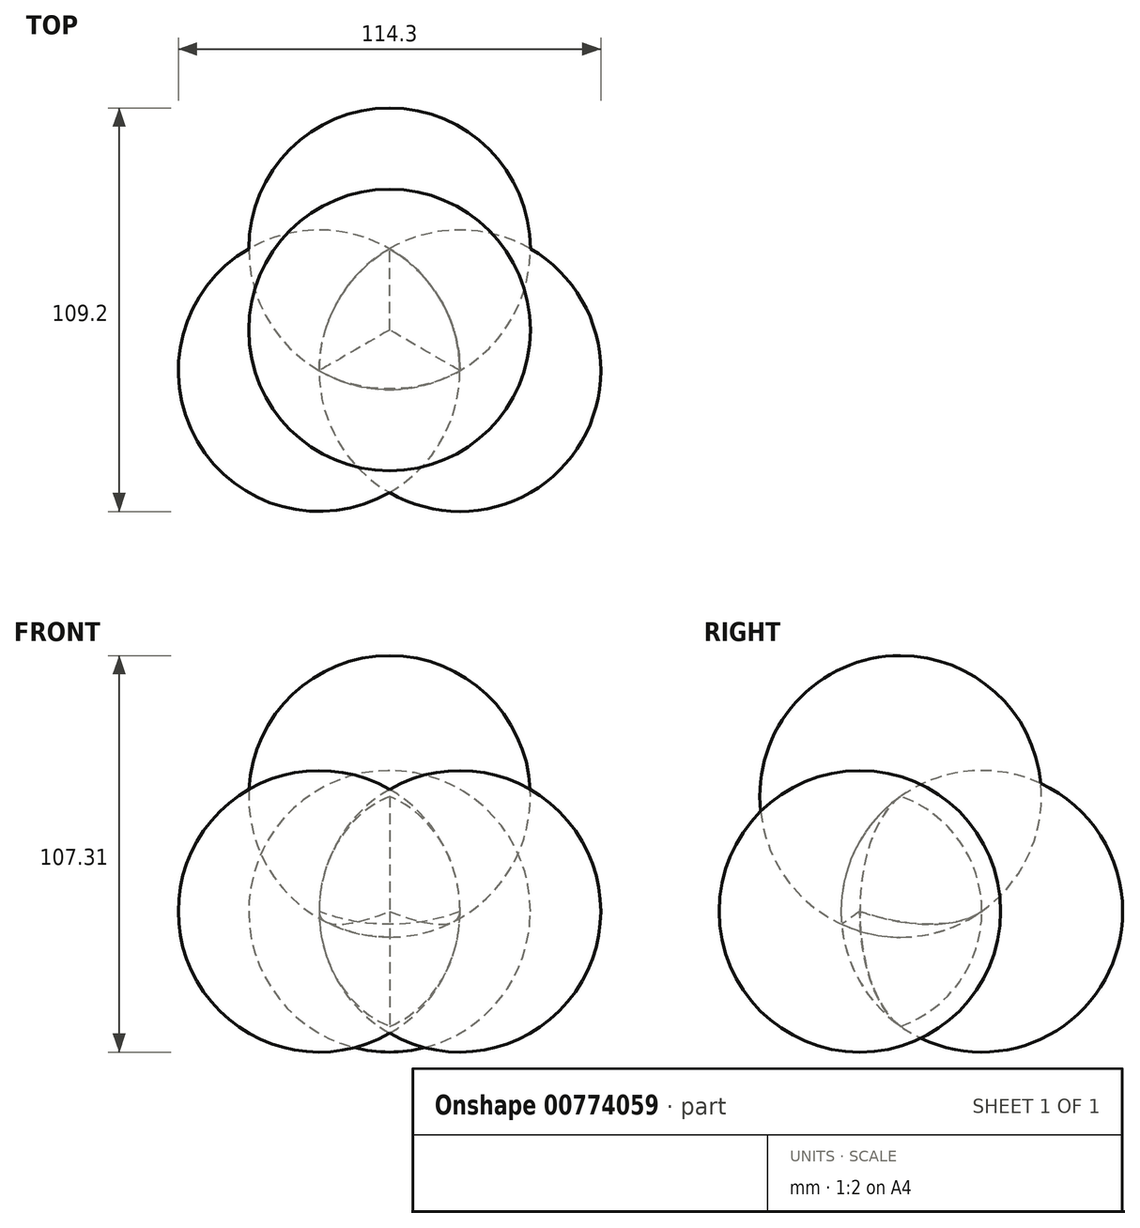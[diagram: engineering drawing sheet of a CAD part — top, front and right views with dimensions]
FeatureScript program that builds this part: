
annotation { "Feature Type Name" : "Feature", "Feature Type Description" : "" }
export const myFeature = defineFeature(function(context is Context, id is Id, definition is map)
    precondition{}
    {
        {
            var Q0;
            Q0=qCreatedBy(makeId("Top.planeOp"),FACE);
            var sketch = newSketch(context, id + "F0", { "sketchPlane" : qUnion([Q0])});
            skLineSegment(sketch, "E0", {"start": v(-19.05, -11) * mm, "end": v(0, 22) * mm, "construction": true});
            skLineSegment(sketch, "E1", {"start": v(0, 22) * mm, "end": v(19.05, -11) * mm, "construction": true});
            skLineSegment(sketch, "E2", {"start": v(19.05, -11) * mm, "end": v(-19.05, -11) * mm, "construction": true});
            skLineSegment(sketch, "E3", {"start": v(0, 0) * mm, "end": v(-19.05, -11) * mm, "construction": true});
            skLineSegment(sketch, "E4", {"start": v(0, 0) * mm, "end": v(0, 22) * mm, "construction": true});
            skLineSegment(sketch, "E5", {"start": v(0, 0) * mm, "end": v(19.05, -11) * mm, "construction": true});
            skSolve(sketch);
        }
        {
            var Q0;
            Q0=qCreatedBy(makeId("Top.planeOp"),FACE);
            var sketch = newSketch(context, id + "F1", { "sketchPlane" : qUnion([Q0])});
            skArc(sketch, "E6", {"start": v(0, -16.1) * mm, "mid": v(38.1, 22) * mm, "end": v(0, 60.1) * mm});
            skLineSegment(sketch, "E7", {"start": v(0, -16.1) * mm, "end": v(0, 60.1) * mm});
            skSolve(sketch);
        }
        {
            var Q0;
            Q0=qCreatedBy(makeId("Top.planeOp"),FACE);
            var sketch = newSketch(context, id + "F2", { "sketchPlane" : qUnion([Q0])});
            skArc(sketch, "E8", {"start": v(38.1, -44) * mm, "mid": v(52.05, 8.05) * mm, "end": v(0, 22) * mm});
            skLineSegment(sketch, "E9", {"start": v(0, 22) * mm, "end": v(38.1, -44) * mm});
            skSolve(sketch);
        }
        {
            var Q0;
            Q0=qCreatedBy(makeId("Top.planeOp"),FACE);
            var sketch = newSketch(context, id + "F3", { "sketchPlane" : qUnion([Q0])});
            skLineSegment(sketch, "E10", {"start": v(-19.05, -11) * mm, "end": v(13.95, 8.05) * mm, "construction": true});
            skArc(sketch, "E11", {"start": v(-52.05, -30.05) * mm, "mid": v(0, -44) * mm, "end": v(13.95, 8.05) * mm});
            skLineSegment(sketch, "E12", {"start": v(-52.05, -30.05) * mm, "end": v(13.95, 8.05) * mm});
            skSolve(sketch);
        }
        {
            var Q0;
            Q0=qCreatedBy(makeId("Front.planeOp"),FACE);
            var sketch = newSketch(context, id + "F4", { "sketchPlane" : qUnion([Q0])});
            skArc(sketch, "E13", {"start": v(0, -7) * mm, "mid": v(38.1, 31.1) * mm, "end": v(0, 69.2) * mm});
            skLineSegment(sketch, "E14", {"start": v(0, 69.2) * mm, "end": v(0, -7) * mm});
            skSolve(sketch);
        }
        {
            var Q0;
            Q0=makeQuery(id+"F4.imprint","IMPRINT",FACE,{"disambiguationData":[TD([[makeQuery(id+"F4.imprint","IMPRINT",EDGE,{"derivedFrom":sQuery(id+"F4.wireOp",EDGE,"E13")}),1.0]])]});
            var Q1;
            Q1=sQuery(id+"F4.wireOp",EDGE,"E14");
            revolve(context, id + "F5", {"surfaceOperationType" : NewSurfaceOperationType.NEW, "entities" : qUnion([Q0]), "axis" : qUnion([Q1]), "revolveType" : RevolveType.FULL});
        }
        {
            var Q0;
            Q0=makeQuery(id+"F1.imprint","IMPRINT",FACE,{"disambiguationData":[TD([[makeQuery(id+"F1.imprint","IMPRINT",EDGE,{"derivedFrom":sQuery(id+"F1.wireOp",EDGE,"E6")}),1.0]])]});
            var Q1;
            Q1=sQuery(id+"F1.wireOp",EDGE,"E7");
            revolve(context, id + "F6", {"surfaceOperationType" : NewSurfaceOperationType.NEW, "entities" : qUnion([Q0]), "axis" : qUnion([Q1]), "revolveType" : RevolveType.FULL});
        }
        {
            var Q0;
            Q0=makeQuery(id+"F2.imprint","IMPRINT",FACE,{"disambiguationData":[TD([[makeQuery(id+"F2.imprint","IMPRINT",EDGE,{"derivedFrom":sQuery(id+"F2.wireOp",EDGE,"E8")}),1.0]])]});
            var Q1;
            Q1=sQuery(id+"F2.wireOp",EDGE,"E9");
            revolve(context, id + "F7", {"surfaceOperationType" : NewSurfaceOperationType.NEW, "entities" : qUnion([Q0]), "axis" : qUnion([Q1]), "revolveType" : RevolveType.FULL});
        }
        {
            var Q0;
            Q0=makeQuery(id+"F3.imprint","IMPRINT",FACE,{"disambiguationData":[TD([[makeQuery(id+"F3.imprint","IMPRINT",EDGE,{"derivedFrom":sQuery(id+"F3.wireOp",EDGE,"E11")}),1.0]])]});
            var Q1;
            Q1=sQuery(id+"F3.wireOp",EDGE,"E12");
            revolve(context, id + "F8", {"surfaceOperationType" : NewSurfaceOperationType.NEW, "entities" : qUnion([Q0]), "axis" : qUnion([Q1]), "revolveType" : RevolveType.FULL});
        }
        {
            var Q0;
            Q0=makeQuery(id+"F5.opRevolve","SWEPT_BODY",BODY,{"disambiguationData":[OSD([sQuery(id+"F4.wireOp",EDGE,"E13"),sQuery(id+"F4.wireOp",EDGE,"E14")])]});
            var Q1;
            Q1=makeQuery(id+"F6.opRevolve","SWEPT_BODY",BODY,{"disambiguationData":[OSD([sQuery(id+"F1.wireOp",EDGE,"E6"),sQuery(id+"F1.wireOp",EDGE,"E7")])]});
            var Q2;
            Q2=makeQuery(id+"F7.opRevolve","SWEPT_BODY",BODY,{"disambiguationData":[OSD([sQuery(id+"F2.wireOp",EDGE,"E8"),sQuery(id+"F2.wireOp",EDGE,"E9")])]});
            var Q3;
            Q3=makeQuery(id+"F8.opRevolve","SWEPT_BODY",BODY,{"disambiguationData":[OSD([sQuery(id+"F3.wireOp",EDGE,"E11"),sQuery(id+"F3.wireOp",EDGE,"E12")])]});
            booleanBodies(context, id + "F9", {"operationType" : BooleanOperationType.INTERSECTION, "tools" : qUnion([Q0, Q1, Q2, Q3]), "keepTools" : true});
        }
        {
            var Q0;
            Q0=makeQuery(id+"F6.opRevolve","SWEPT_BODY",BODY,{"disambiguationData":[OSD([sQuery(id+"F1.wireOp",EDGE,"E6"),sQuery(id+"F1.wireOp",EDGE,"E7")])]});
            var Q1;
            Q1=makeQuery(id+"F7.opRevolve","SWEPT_BODY",BODY,{"disambiguationData":[OSD([sQuery(id+"F2.wireOp",EDGE,"E8"),sQuery(id+"F2.wireOp",EDGE,"E9")])]});
            var Q2;
            Q2=makeQuery(id+"F8.opRevolve","SWEPT_BODY",BODY,{"disambiguationData":[OSD([sQuery(id+"F3.wireOp",EDGE,"E11"),sQuery(id+"F3.wireOp",EDGE,"E12")])]});
            booleanBodies(context, id + "F10", {"operationType" : BooleanOperationType.INTERSECTION, "tools" : qUnion([Q0, Q1, Q2]), "keepTools" : true});
        }
    });
